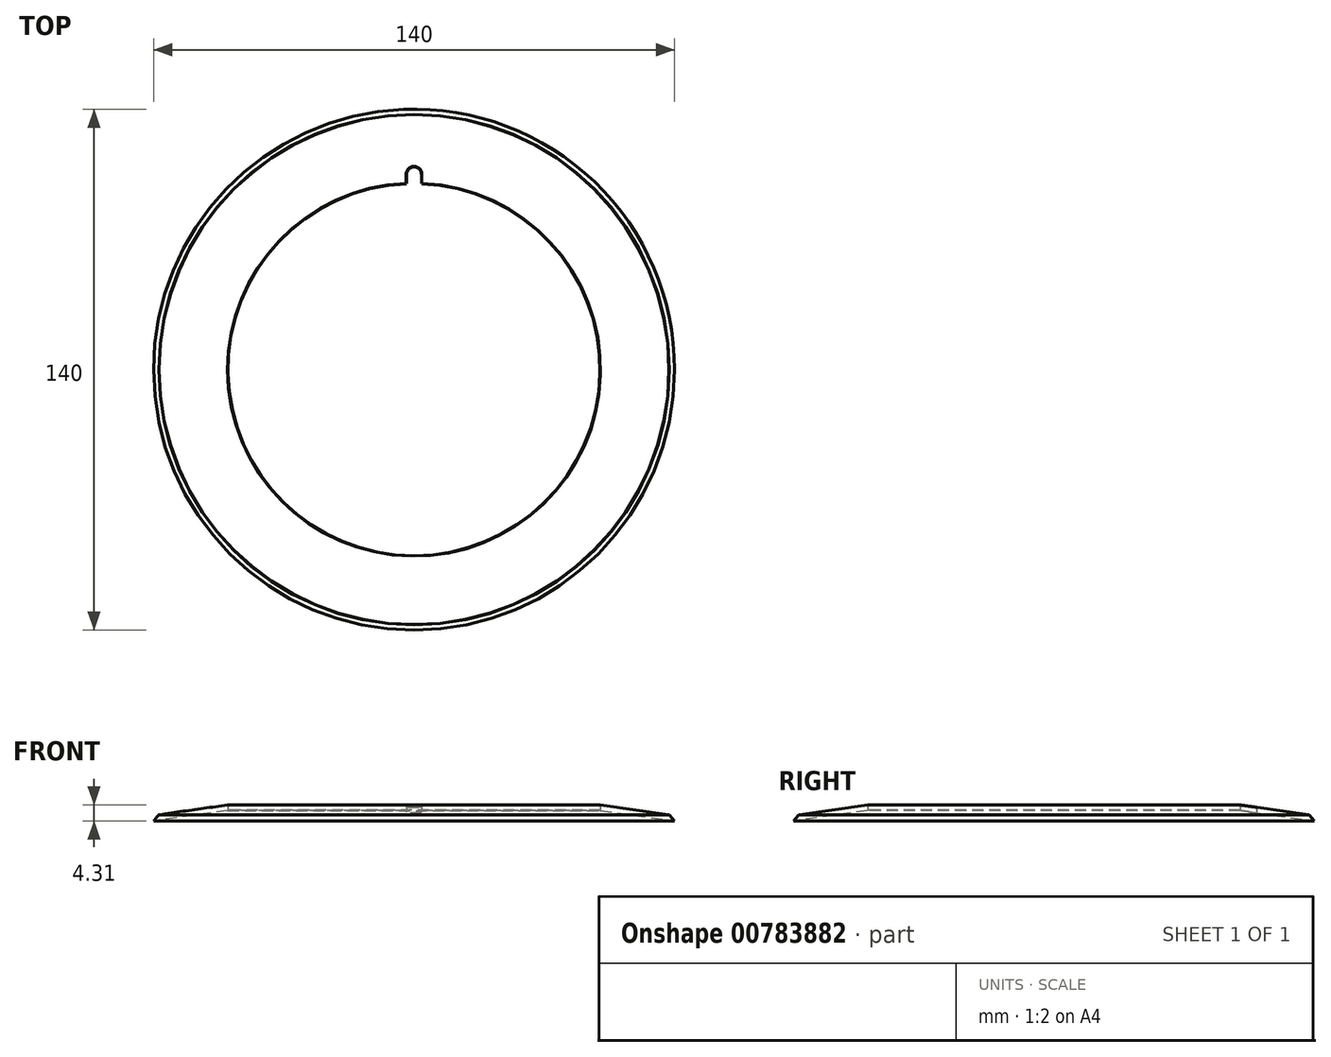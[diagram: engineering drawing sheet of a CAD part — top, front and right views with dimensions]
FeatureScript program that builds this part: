
annotation { "Feature Type Name" : "Feature", "Feature Type Description" : "" }
export const myFeature = defineFeature(function(context is Context, id is Id, definition is map)
    precondition{}
    {
        {
            var Q0;
            Q0=qCreatedBy(makeId("Front.planeOp"),FACE);
            var sketch = newSketch(context, id + "F0", { "sketchPlane" : qUnion([Q0])});
            skLineSegment(sketch, "E0", {"start": v(70, 0) * mm, "end": v(70, 1.51) * mm});
            skLineSegment(sketch, "E1", {"start": v(70, 1.51) * mm, "end": v(50, 4.33) * mm});
            skLineSegment(sketch, "E2", {"start": v(50, 4.33) * mm, "end": v(50, 2.81) * mm});
            skLineSegment(sketch, "E3", {"start": v(50, 2.81) * mm, "end": v(70, 0) * mm});
            skLineSegment(sketch, "E4", {"start": v(0, 0) * mm, "end": v(0, 11.85) * mm, "construction": true});
            skSolve(sketch);
        }
        {
            var Q0;
            Q0=makeQuery(id+"F0.imprint","IMPRINT",FACE,{"disambiguationData":[TD([[makeQuery(id+"F0.imprint","IMPRINT",EDGE,{"derivedFrom":sQuery(id+"F0.wireOp",EDGE,"E0")}),1.0]])]});
            var Q1;
            Q1=sQuery(id+"F0.wireOp",EDGE,"E4");
            revolve(context, id + "F1", {"surfaceOperationType" : NewSurfaceOperationType.NEW, "entities" : qUnion([Q0]), "axis" : qUnion([Q1]), "revolveType" : RevolveType.FULL});
        }
        {
            var Q0;
            Q0=qCreatedBy(makeId("Front.planeOp"),FACE);
            var sketch = newSketch(context, id + "F2", { "sketchPlane" : qUnion([Q0])});
            skLineSegment(sketch, "E5.0", {"start": v(70, 0) * mm, "end": v(-70, 0) * mm, "construction": true});
            skCircle(sketch, "E6", {"center": v(70, 0) * mm, "radius": 2.5 * mm, "construction": true});
            skLineSegment(sketch, "E7", {"start": v(70, 0) * mm, "end": v(65.64, 5.2) * mm});
            skLineSegment(sketch, "E8", {"start": v(65.64, 5.2) * mm, "end": v(73.07, 5.2) * mm});
            skLineSegment(sketch, "E9", {"start": v(73.07, 5.2) * mm, "end": v(73.07, 0) * mm});
            skLineSegment(sketch, "E10", {"start": v(73.07, 0) * mm, "end": v(70, 0) * mm});
            skLineSegment(sketch, "E11", {"start": v(0, 0) * mm, "end": v(0, 20.01) * mm, "construction": true});
            skSolve(sketch);
        }
        {
            var Q0;
            Q0=makeQuery(id+"F2.imprint","IMPRINT",FACE,{"disambiguationData":[TD([[makeQuery(id+"F2.imprint","IMPRINT",EDGE,{"derivedFrom":sQuery(id+"F2.wireOp",EDGE,"E7")}),-1.0]])]});
            var Q1;
            Q1=sQuery(id+"F2.wireOp",EDGE,"E11");
            revolve(context, id + "F3", {"operationType" : NewBodyOperationType.REMOVE, "surfaceOperationType" : NewSurfaceOperationType.NEW, "entities" : qUnion([Q0]), "axis" : qUnion([Q1]), "revolveType" : RevolveType.FULL, "oppositeDirection" : true});
        }
        {
            var Q0;
            Q0=qCreatedBy(makeId("Top.planeOp"),FACE);
            var sketch = newSketch(context, id + "F4", { "sketchPlane" : qUnion([Q0])});
            skCircle(sketch, "E12.0", {"center": v(0, 0) * mm, "radius": 50 * mm});
            skLineSegment(sketch, "E13.bottom", {"start": v(2, 52.5) * mm, "end": v(-2, 52.5) * mm});
            skLineSegment(sketch, "E13.top", {"start": v(2, 33.02) * mm, "end": v(-2, 33.02) * mm});
            skLineSegment(sketch, "E13.left", {"start": v(2, 52.5) * mm, "end": v(2, 33.02) * mm});
            skLineSegment(sketch, "E13.right", {"start": v(-2, 52.5) * mm, "end": v(-2, 33.02) * mm});
            skPoint(sketch, "E13.middle", {"position": v(0, 42.76) * mm});
            skArc(sketch, "E14", {"start": v(2, 52.5) * mm, "mid": v(0, 54.5) * mm, "end": v(-2, 52.5) * mm});
            skSolve(sketch);
        }
        {
            var Q0;
            {var subQ5=sQuery(id+"F4.wireOp",EDGE,"E13.bottom");Q0=makeQuery(id+"F4.imprint","IMPRINT",FACE,{"disambiguationData":[TD([[makeQuery(id+"F4.imprint","IMPRINT",EDGE,{"derivedFrom":subQ5}),1.0]])]});}
            var Q1;
            Q1=makeQuery(id+"F4.imprint","IMPRINT",FACE,{"disambiguationData":[TD([[makeQuery(id+"F4.imprint","IMPRINT",EDGE,{"derivedFrom":sQuery(id+"F4.wireOp",EDGE,"E13.bottom")}),-1.0]])]});
            extrude(context, id + "F5", {"entities" : qUnion([Q0, Q1]), "operationType" : NewBodyOperationType.REMOVE, "endBound" : BoundingType.THROUGH_ALL, "depth" : 25 * mm, "offsetDistance" : 25 * mm});
        }
        {
            var Q0;
            Q0=makeQuery(id+"F1.opRevolve","SWEPT_FACE",FACE,{"disambiguationData":[OSD([sQuery(id+"F0.wireOp",EDGE,"E1")])]});
            var Q1;
            Q1=makeQuery(id+"F1.opRevolve","SWEPT_EDGE",EDGE,{"disambiguationData":[OSD([sQuery(id+"F0.wireOp",EDGE,"E2"),sQuery(id+"F0.wireOp",EDGE,"E3")])]});
            chamfer(context, id + "F6", {"entities" : qUnion([Q0, Q1]), "width" : 0.1 * mm, "tangentPropagation" : true});
        }
    });
